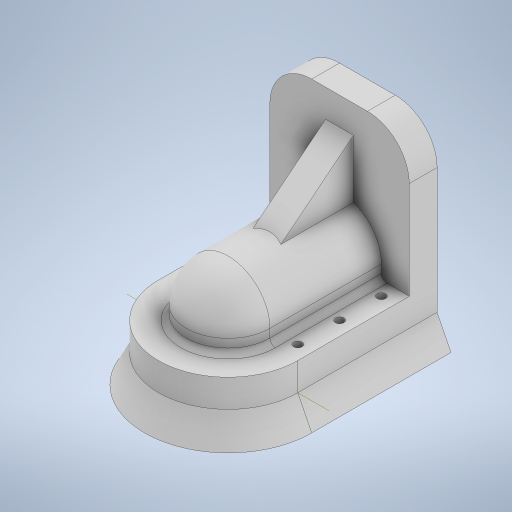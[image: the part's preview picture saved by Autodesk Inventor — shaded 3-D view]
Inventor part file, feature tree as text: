
AUTODESK INVENTOR PART (.ipt)
format: ipt  version: 2024 (Build 280153000, 153)  size: 411,648 bytes
history: native  units: mm
features: sketch x12, extrude x8, fillet x3, other x2, plane x1, loft x1, rib x1, revolve x1
ambient origin geometry x8: Origin, YZ Plane, XZ Plane, XY Plane, X Axis, Y Axis, Z Axis, Center Point
bodies: Body1 (feature_tree)
feature tree (29):
  sketch  "Sketch1"  dims[d3=10.0mm d11=50.0mm]
  plane  "Work Plane1"
  extrude  "Extrusion1"  Depth=50.0mm
  loft  "Loft2"
  extrude  "Extrusion2"  TaperAngle=0.0deg  [1 undecoded]
  fillet  "Fillet1"  Radius=50.0mm
  extrude  "Extrusion3"  Depth=50.0mm TaperAngle=0.0deg
  extrude  "Extrusion4"  Depth=30.0mm
  fillet  "Fillet2"  Radius=40.0mm
  fillet  "Fillet3"  Radius=20.0mm
  rib  "Rib1"
  extrude  "Extrusion5"  Depth=15.0mm
  extrude  "Extrusion6"  Depth=10.0mm
  extrude  "Extrusion7"  Depth=3.0mm
  sketch  "Sketch24"  dims[d45=5.0mm d46=15.0mm]
  sketch  "Sketch25"  dims[d47=15.0mm d48=5.0mm]
  extrude  "Extrusion8"  Depth=15.0mm
  other  "Work Axis3"
  revolve  "Revolution1"  [1 undecoded]
  sketch  "Sketch5"  dims[d12=50.0mm d13=10.0mm d14=0.0mm]
  other  "Edges1"
  sketch  "Sketch6"  dims[d15=0.0mm d16=90.0deg d17=0.0mm d18=90.0deg d19=50.0mm]
  sketch  "Sketch7"  dims[d20=10.0mm d21=50.0mm d22=0.0mm]
  sketch  "Sketch8"  dims[d23=15.0mm d24=30.0mm d25=40.0mm d26=20.0mm d27=0.0mm]
  sketch  "Sketch12"  dims[d28=20.0mm d29=0.0mm d30=15.0mm]
  sketch  "Sketch14"  dims[d31=2.0mm]
  sketch  "Sketch15"  dims[d36=1.0mm d37=10.0mm d38=0.0mm d39=0.0mm d40=1.0mm d41=1.0mm d42=3.0mm]
  sketch  "Sketch18"  dims[d43=3.0mm d44=3.0mm]
  sketch  "Sketch26"  dims[d49=5.0mm d50=5.0mm d51=3.0mm d52=3.0mm d53=3.0mm d60=20.0mm d61=0.0mm d62=3.0mm d63=3.0mm d64=3.0mm d65=15.0mm d66=5.0mm d67=15.0mm d70=20.0mm d71=0.0mm d72=10.0mm d73=10.0mm d74=5.0mm d75=5.0mm d76=5.0mm d77=5.0mm d78=5.0mm d79=5.0mm d92=50.0mm d93=0.0mm d95=10.0mm d96=0.0mm d97=90.0deg d54=0.15mm d55=0.25mm d56=0.375mm d57=14.3117mm d58=0.75mm d59=20.594885mm d83=0.5mm d84=0.872665mm d85=0.5mm d86=0.872665mm d98=0.872665mm]
note: 2 required parameter values undecoded (feature->parameter linkage not recoverable at this tier; creation-order binding heuristic only, values carry confidence <= 0.55)